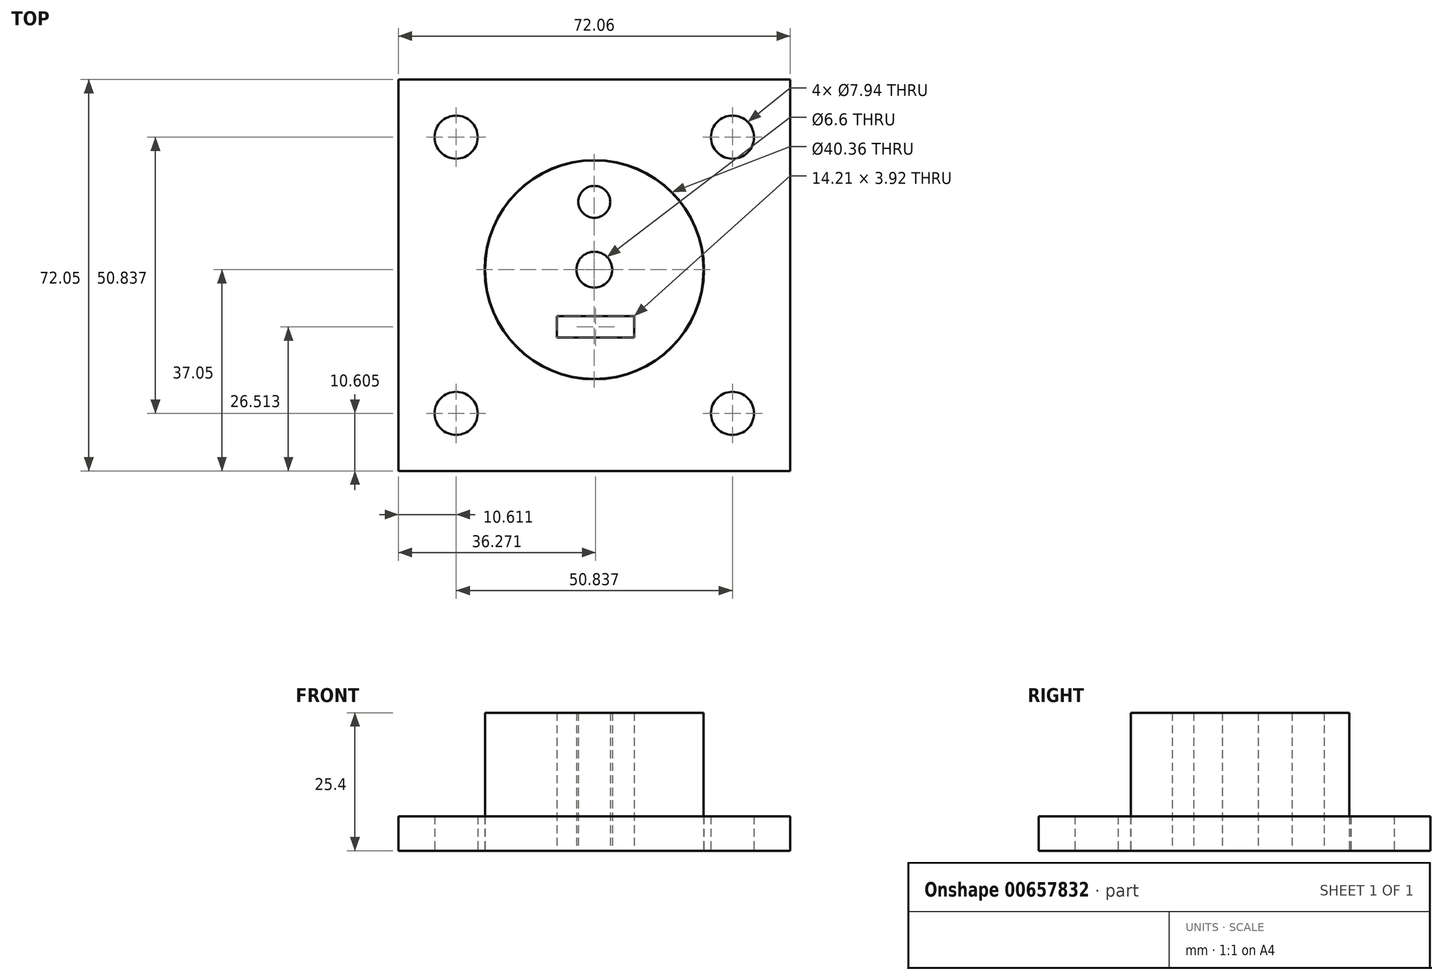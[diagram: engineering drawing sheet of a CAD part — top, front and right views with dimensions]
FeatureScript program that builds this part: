
annotation { "Feature Type Name" : "Feature", "Feature Type Description" : "" }
export const myFeature = defineFeature(function(context is Context, id is Id, definition is map)
    precondition{}
    {
        {
            var Q0;
            Q0=qCreatedBy(makeId("Top.planeOp"),FACE);
            var sketch = newSketch(context, id + "F0", { "sketchPlane" : qUnion([Q0])});
            skLineSegment(sketch, "E0.bottom", {"start": v(-36.03, 35) * mm, "end": v(36.03, 35) * mm});
            skLineSegment(sketch, "E0.top", {"start": v(-36.03, -37.05) * mm, "end": v(36.03, -37.05) * mm});
            skLineSegment(sketch, "E0.left", {"start": v(-36.03, 35) * mm, "end": v(-36.03, -37.05) * mm});
            skLineSegment(sketch, "E0.right", {"start": v(36.03, 35) * mm, "end": v(36.03, -37.05) * mm});
            skCircle(sketch, "E1", {"center": v(0, 0) * mm, "radius": 20.18 * mm});
            skLineSegment(sketch, "E2", {"start": v(0, 0) * mm, "end": v(-36.03, 0) * mm, "construction": true});
            skLineSegment(sketch, "E3", {"start": v(-36.03, 0) * mm, "end": v(0, 0) * mm, "construction": true});
            skLineSegment(sketch, "E4", {"start": v(0, 0) * mm, "end": v(36.03, 0) * mm, "construction": true});
            skLineSegment(sketch, "E5", {"start": v(-36.03, 24.4) * mm, "end": v(-25.42, 24.4) * mm, "construction": true});
            skLineSegment(sketch, "E6", {"start": v(-25.42, 35) * mm, "end": v(-25.42, 24.4) * mm, "construction": true});
            skLineSegment(sketch, "E7", {"start": v(36.03, 24.4) * mm, "end": v(25.42, 24.4) * mm, "construction": true});
            skLineSegment(sketch, "E8", {"start": v(25.42, 24.4) * mm, "end": v(25.42, 35) * mm, "construction": true});
            skLineSegment(sketch, "E9", {"start": v(36.03, -26.44) * mm, "end": v(25.42, -26.44) * mm, "construction": true});
            skLineSegment(sketch, "E10", {"start": v(25.42, -26.44) * mm, "end": v(25.42, -37.05) * mm, "construction": true});
            skLineSegment(sketch, "E11", {"start": v(25.42, -37.05) * mm, "end": v(-25.42, -37.05) * mm, "construction": true});
            skLineSegment(sketch, "E12", {"start": v(-25.42, -37.05) * mm, "end": v(-25.42, -26.44) * mm, "construction": true});
            skLineSegment(sketch, "E13", {"start": v(-25.42, -26.44) * mm, "end": v(-36.03, -26.44) * mm, "construction": true});
            skCircle(sketch, "E14", {"center": v(-25.42, 24.4) * mm, "radius": 3.97 * mm});
            skCircle(sketch, "E15", {"center": v(25.42, 24.4) * mm, "radius": 3.97 * mm});
            skCircle(sketch, "E16", {"center": v(25.42, -26.44) * mm, "radius": 3.97 * mm});
            skCircle(sketch, "E17", {"center": v(-25.42, -26.44) * mm, "radius": 3.97 * mm});
            skCircle(sketch, "E18", {"center": v(0, 0) * mm, "radius": 5.02 * mm});
            skLineSegment(sketch, "E19", {"start": v(0, 0) * mm, "end": v(0, 20.18) * mm, "construction": true});
            skPoint(sketch, "E19.endSnap0", {"position": v(0, 35) * mm});
            skCircle(sketch, "E20", {"center": v(0, 12.99) * mm, "radius": 2.25 * mm});
            skLineSegment(sketch, "E21", {"start": v(0, -20.18) * mm, "end": v(0, -5.02) * mm, "construction": true});
            skPoint(sketch, "E22.oppositeSnap0", {"position": v(0, -12.6) * mm});
            skLineSegment(sketch, "E22.bottom", {"start": v(-6.8, -9.31) * mm, "end": v(6.8, -9.31) * mm});
            skLineSegment(sketch, "E22.top", {"start": v(-6.8, -12.6) * mm, "end": v(6.8, -12.6) * mm});
            skLineSegment(sketch, "E22.left", {"start": v(-6.8, -9.31) * mm, "end": v(-6.8, -12.6) * mm});
            skLineSegment(sketch, "E22.right", {"start": v(6.8, -9.31) * mm, "end": v(6.8, -12.6) * mm});
            skLineSegment(sketch, "E23", {"start": v(0, -9.31) * mm, "end": v(6.8, -9.31) * mm, "construction": true});
            skLineSegment(sketch, "E24", {"start": v(0, -9.31) * mm, "end": v(-6.8, -9.31) * mm, "construction": true});
            skCircle(sketch, "E25", {"center": v(0, 0) * mm, "radius": 23.41 * mm});
            skSolve(sketch);
        }
        {
            var Q0;
            Q0=makeQuery(id+"F0.imprint","IMPRINT",FACE,{"disambiguationData":[TD([[makeQuery(id+"F0.imprint","IMPRINT",EDGE,{"derivedFrom":sQuery(id+"F0.wireOp",EDGE,"E0.bottom")}),-1.0]])]});
            var Q1;
            Q1=makeQuery(id+"F0.imprint","IMPRINT",FACE,{"disambiguationData":[TD([[makeQuery(id+"F0.imprint","IMPRINT",EDGE,{"derivedFrom":sQuery(id+"F0.wireOp",EDGE,"E1")}),-1.0]])]});
            extrude(context, id + "F1", {"entities" : qUnion([Q0, Q1]), "depth" : 6.35 * mm, "offsetDistance" : 25.4 * mm});
        }
        {
            var Q0;
            Q0=qCreatedBy(makeId("Top.planeOp"),FACE);
            var sketch = newSketch(context, id + "F2", { "sketchPlane" : qUnion([Q0])});
            skCircle(sketch, "E26", {"center": v(0, 0) * mm, "radius": 24.07 * mm});
            skCircle(sketch, "E27", {"center": v(0, 0) * mm, "radius": 3.3 * mm});
            skLineSegment(sketch, "E28.bottom", {"start": v(7.35, -8.58) * mm, "end": v(-6.87, -8.58) * mm});
            skLineSegment(sketch, "E28.top", {"start": v(7.35, -12.5) * mm, "end": v(-6.87, -12.5) * mm});
            skLineSegment(sketch, "E28.left", {"start": v(7.35, -8.58) * mm, "end": v(7.35, -12.5) * mm});
            skLineSegment(sketch, "E28.right", {"start": v(-6.87, -8.58) * mm, "end": v(-6.87, -12.5) * mm});
            skCircle(sketch, "E29", {"center": v(0, 12.5) * mm, "radius": 2.94 * mm});
            skLineSegment(sketch, "E30", {"start": v(0, 0) * mm, "end": v(3.3, 0) * mm, "construction": true});
            skLineSegment(sketch, "E31", {"start": v(0, 0) * mm, "end": v(-3.3, 0) * mm, "construction": true});
            skCircle(sketch, "E32", {"center": v(0, 0) * mm, "radius": 20.1 * mm});
            skLineSegment(sketch, "E33", {"start": v(0, 0) * mm, "end": v(20.1, 0) * mm, "construction": true});
            skSolve(sketch);
        }
        {
            var Q0;
            Q0=makeQuery(id+"F2.imprint","IMPRINT",FACE,{"disambiguationData":[TD([[makeQuery(id+"F2.imprint","IMPRINT",EDGE,{"derivedFrom":sQuery(id+"F2.wireOp",EDGE,"E27")}),-1.0]])]});
            extrude(context, id + "F3", {"entities" : qUnion([Q0]), "depth" : 25.4 * mm, "offsetDistance" : 25.4 * mm});
        }
    });
